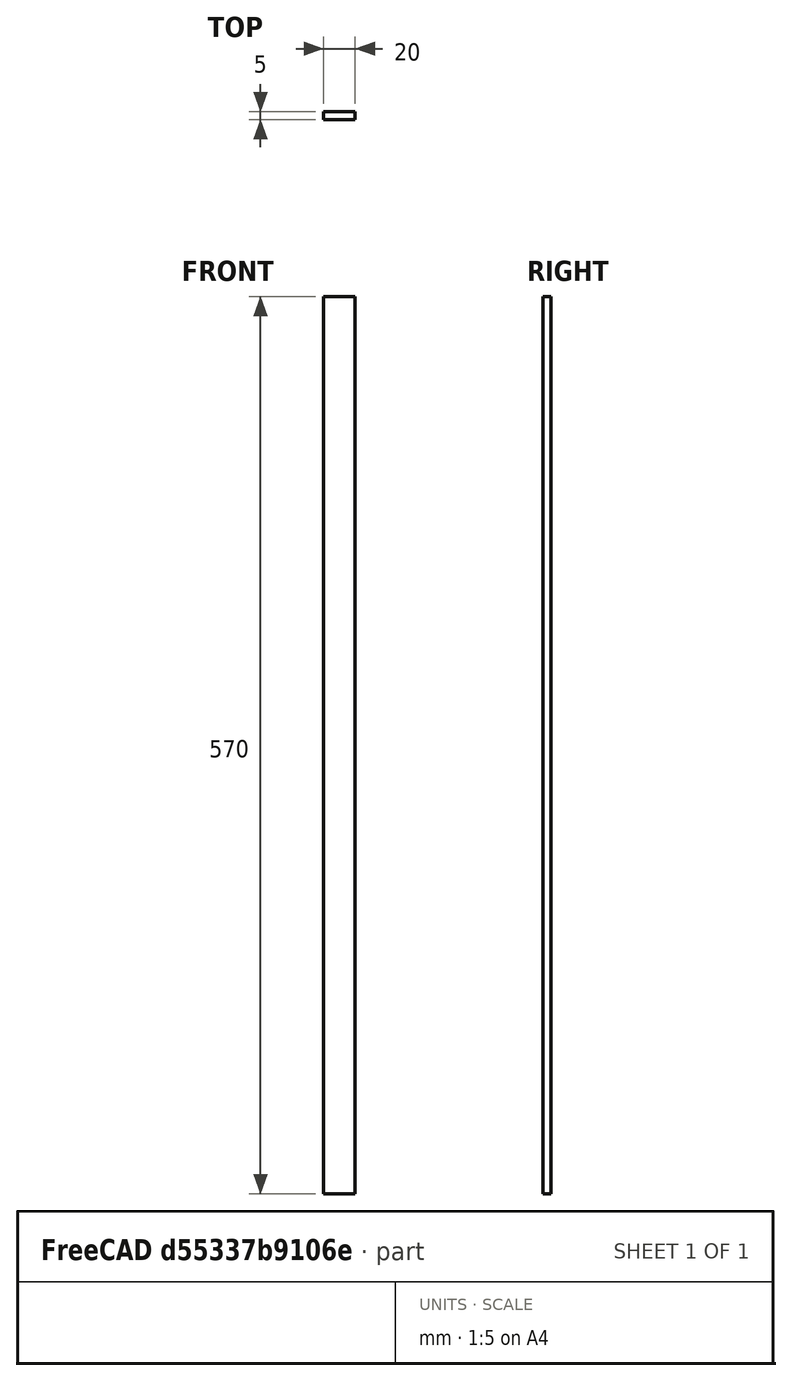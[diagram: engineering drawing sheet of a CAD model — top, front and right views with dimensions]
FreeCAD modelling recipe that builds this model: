
FCSTD DOCUMENT  (FreeCAD 0.19R24276 (Git))
Label: L570
License: All rights reserved
LicenseURL: http://en.wikipedia.org/wiki/All_rights_reserved
objects: Sketcher::SketchObject×1, PartDesign::Pad×1, PartDesign::Body×1
note: 4 computed .brp shape members not serialized (recipe doc carries the construction recipe); baked Part::Feature solids carry a one-line shape summary decoded from their .brp

FEATURE [Sketcher::SketchObject] Sketch
  FullyConstrained = true
  MapMode = 5
  Support = -> [XY_Plane]
  sketch-geometry (4):
    g0: LineSegment StartX=0 StartY=0 StartZ=0 EndX=20 EndY=0 EndZ=0
    g1: LineSegment StartX=20 StartY=0 StartZ=0 EndX=20 EndY=-5 EndZ=0
    g2: LineSegment StartX=20 StartY=-5 StartZ=0 EndX=0 EndY=-5 EndZ=0
    g3: LineSegment StartX=0 StartY=-5 StartZ=0 EndX=0 EndY=0 EndZ=0
  constraints (11):
    c: Coincident(g0,g1)
    c: Coincident(g1,g2)
    c: Coincident(g2,g3)
    c: Coincident(g3,g0)
    c: Horizontal(g0)
    c: Horizontal(g2)
    c: Vertical(g1)
    c: Vertical(g3)
    c: Coincident(g0,g-1)
    c: DistanceY(g1,g1) = 5
    c: DistanceX(g2,g2) = 20
FEATURE [PartDesign::Pad] Pad
  Direction = (1,1,1)
  Length = 570
  Length2 = 100
  Profile = -> Sketch
  Type = 0
FEATURE [PartDesign::Body] Body
  Group = -> [Sketch,Pad]
  Origin = -> Origin
  Tip = -> Pad
